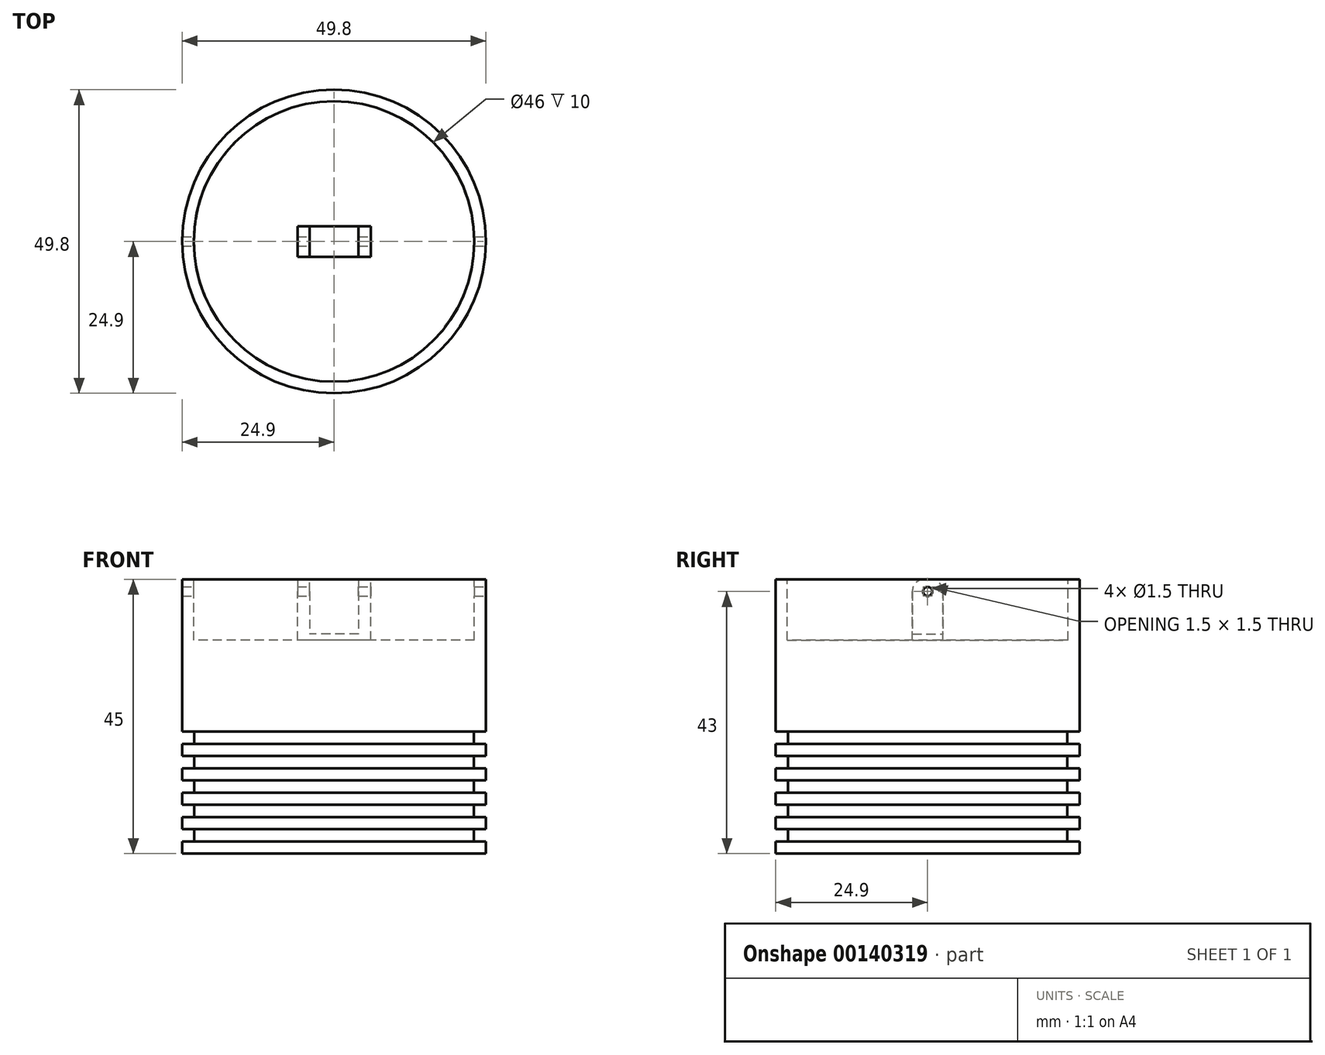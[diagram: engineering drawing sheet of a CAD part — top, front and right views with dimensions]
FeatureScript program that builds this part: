
annotation { "Feature Type Name" : "Feature", "Feature Type Description" : "" }
export const myFeature = defineFeature(function(context is Context, id is Id, definition is map)
    precondition{}
    {
        {
            var Q0;
            Q0=qCreatedBy(makeId("Front.planeOp"),FACE);
            var sketch = newSketch(context, id + "F0", { "sketchPlane" : qUnion([Q0])});
            skLineSegment(sketch, "E0.bottom", {"start": v(0, 0) * mm, "end": v(24.9, 0) * mm});
            skLineSegment(sketch, "E0.top", {"start": v(0, 45) * mm, "end": v(24.9, 45) * mm});
            skLineSegment(sketch, "E0.left", {"start": v(0, 0) * mm, "end": v(0, 45) * mm});
            skLineSegment(sketch, "E0.right", {"start": v(24.9, 0) * mm, "end": v(24.9, 45) * mm, "construction": true});
            skLineSegment(sketch, "E1", {"start": v(24.9, 0) * mm, "end": v(24.9, 2) * mm});
            skLineSegment(sketch, "E2", {"start": v(24.9, 2) * mm, "end": v(22.9, 2) * mm});
            skLineSegment(sketch, "E3", {"start": v(22.9, 2) * mm, "end": v(22.9, 4) * mm});
            skLineSegment(sketch, "E4", {"start": v(22.9, 4) * mm, "end": v(24.9, 4) * mm});
            skLineSegment(sketch, "E5.0.1.0", {"start": v(24.9, 6) * mm, "end": v(22.9, 6) * mm});
            skLineSegment(sketch, "E5.0.1.1", {"start": v(24.9, 4) * mm, "end": v(24.9, 6) * mm});
            skLineSegment(sketch, "E5.0.1.2", {"start": v(22.9, 8) * mm, "end": v(24.9, 8) * mm});
            skLineSegment(sketch, "E5.0.1.3", {"start": v(22.9, 6) * mm, "end": v(22.9, 8) * mm});
            skLineSegment(sketch, "E5.direction1", {"start": v(24.9, 0) * mm, "end": v(50, 0) * mm, "construction": true});
            skLineSegment(sketch, "E5.direction2", {"start": v(24.9, 0) * mm, "end": v(24.9, 4) * mm, "construction": true});
            skLineSegment(sketch, "E6.0.0.2", {"start": v(24.9, 10) * mm, "end": v(22.9, 10) * mm});
            skLineSegment(sketch, "E6.3.0.2", {"start": v(24.9, 8) * mm, "end": v(24.9, 10) * mm});
            skLineSegment(sketch, "E6.6.0.2", {"start": v(22.9, 12) * mm, "end": v(24.9, 12) * mm});
            skLineSegment(sketch, "E6.9.0.2", {"start": v(22.9, 10) * mm, "end": v(22.9, 12) * mm});
            skLineSegment(sketch, "E6.0.0.3", {"start": v(24.9, 14) * mm, "end": v(22.9, 14) * mm});
            skLineSegment(sketch, "E6.3.0.3", {"start": v(24.9, 12) * mm, "end": v(24.9, 14) * mm});
            skLineSegment(sketch, "E6.6.0.3", {"start": v(22.9, 16) * mm, "end": v(24.9, 16) * mm});
            skLineSegment(sketch, "E6.9.0.3", {"start": v(22.9, 14) * mm, "end": v(22.9, 16) * mm});
            skLineSegment(sketch, "E6.0.0.4", {"start": v(24.9, 18) * mm, "end": v(22.9, 18) * mm});
            skLineSegment(sketch, "E6.3.0.4", {"start": v(24.9, 16) * mm, "end": v(24.9, 18) * mm});
            skLineSegment(sketch, "E6.6.0.4", {"start": v(22.9, 20) * mm, "end": v(24.9, 20) * mm});
            skLineSegment(sketch, "E6.9.0.4", {"start": v(22.9, 18) * mm, "end": v(22.9, 20) * mm});
            skLineSegment(sketch, "E7", {"start": v(24.9, 20) * mm, "end": v(24.9, 45) * mm});
            skSolve(sketch);
        }
        {
            var Q0;
            Q0=makeQuery(id+"F0.imprint","IMPRINT",FACE,{"disambiguationData":[TD([[makeQuery(id+"F0.imprint","IMPRINT",EDGE,{"derivedFrom":sQuery(id+"F0.wireOp",EDGE,"E0.bottom")}),1.0]])]});
            var Q1;
            Q1=sQuery(id+"F0.wireOp",EDGE,"E0.left");
            revolve(context, id + "F1", {"entities" : qUnion([Q0]), "axis" : qUnion([Q1]), "revolveType" : RevolveType.FULL});
        }
        {
            var Q0;
            Q0=makeQuery(id+"F1.opRevolve","SWEPT_FACE",FACE,{"disambiguationData":[OSD([sQuery(id+"F0.wireOp",EDGE,"E0.top")])]});
            var sketch = newSketch(context, id + "F2", { "sketchPlane" : qUnion([Q0])});
            skCircle(sketch, "E8", {"center": v(0, 0) * mm, "radius": 23 * mm});
            skSolve(sketch);
        }
        {
            var Q0;
            Q0 = qSketchRegion(id + "F2", true);
            extrude(context, id + "F3", {"entities" : qUnion([Q0]), "operationType" : NewBodyOperationType.REMOVE, "oppositeDirection" : true, "depth" : 10 * mm});
        }
        {
            var Q0;
            Q0=qCreatedBy(makeId("Front.planeOp"),FACE);
            var sketch = newSketch(context, id + "F4", { "sketchPlane" : qUnion([Q0])});
            skPoint(sketch, "E9", {"position": v(0, 45) * mm});
            skPoint(sketch, "E10", {"position": v(0, 35) * mm});
            skLineSegment(sketch, "E11", {"start": v(0, 35) * mm, "end": v(6, 35) * mm});
            skLineSegment(sketch, "E12", {"start": v(6, 35) * mm, "end": v(6, 45) * mm});
            skLineSegment(sketch, "E13", {"start": v(6, 45) * mm, "end": v(4, 45) * mm});
            skLineSegment(sketch, "E14", {"start": v(4, 45) * mm, "end": v(4, 36) * mm});
            skLineSegment(sketch, "E15", {"start": v(4, 36) * mm, "end": v(0, 36) * mm});
            skLineSegment(sketch, "E16.MirrorCS", {"start": v(-4, 36) * mm, "end": v(0, 36) * mm});
            skLineSegment(sketch, "E17.MirrorCS", {"start": v(-4, 45) * mm, "end": v(-4, 36) * mm});
            skLineSegment(sketch, "E18.MirrorCS", {"start": v(-6, 45) * mm, "end": v(-4, 45) * mm});
            skLineSegment(sketch, "E19.MirrorCS", {"start": v(-6, 35) * mm, "end": v(-6, 45) * mm});
            skLineSegment(sketch, "E20.MirrorCS", {"start": v(0, 35) * mm, "end": v(-6, 35) * mm});
            skSolve(sketch);
        }
        {
            var Q0;
            Q0 = qSketchRegion(id + "F4", true);
            extrude(context, id + "F5", {"entities" : qUnion([Q0]), "endBound" : BoundingType.SYMMETRIC, "depth" : 5 * mm});
        }
        {
            var Q0;
            Q0=makeQuery(id+"F5.opExtrude","SWEPT_FACE",FACE,{"disambiguationData":[OSD([sQuery(id+"F4.wireOp",EDGE,"E17.MirrorCS")])]});
            var sketch = newSketch(context, id + "F6", { "sketchPlane" : qUnion([Q0])});
            skCircle(sketch, "E21", {"center": v(0, 43) * mm, "radius": 0.75 * mm});
            skSolve(sketch);
        }
        {
            var Q0;
            Q0 = qSketchRegion(id + "F6", true);
            extrude(context, id + "F7", {"entities" : qUnion([Q0]), "operationType" : NewBodyOperationType.REMOVE, "endBound" : BoundingType.SYMMETRIC, "oppositeDirection" : true, "depth" : 100 * mm});
        }
        {
            var Q0;
            Q0=makeQuery(id+"F5.opExtrude","CAP_EDGE",EDGE,{"disambiguationData":[OSD([sQuery(id+"F4.wireOp",EDGE,"E18.MirrorCS")])],"isStart":false});
            var Q1;
            Q1=makeQuery(id+"F5.opExtrude","CAP_EDGE",EDGE,{"disambiguationData":[OSD([sQuery(id+"F4.wireOp",EDGE,"E18.MirrorCS")])],"isStart":true});
            var Q2;
            Q2=makeQuery(id+"F5.opExtrude","CAP_EDGE",EDGE,{"disambiguationData":[OSD([sQuery(id+"F4.wireOp",EDGE,"E13")])],"isStart":true});
            var Q3;
            Q3=makeQuery(id+"F5.opExtrude","CAP_EDGE",EDGE,{"disambiguationData":[OSD([sQuery(id+"F4.wireOp",EDGE,"E13")])],"isStart":false});
            fillet(context, id + "F8", {"entities" : qUnion([Q0, Q1, Q2, Q3]), "radius" : 2 * mm, "tangentPropagation" : true, "allowEdgeOverflow" : false});
        }
    });
